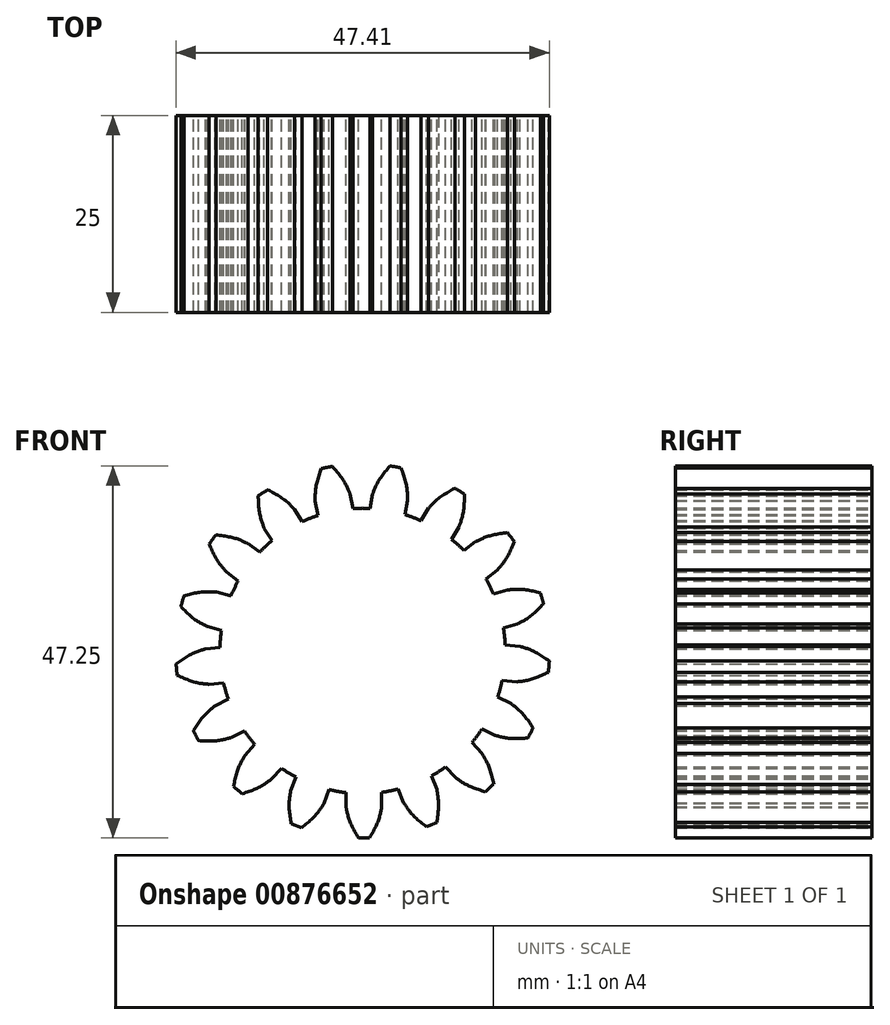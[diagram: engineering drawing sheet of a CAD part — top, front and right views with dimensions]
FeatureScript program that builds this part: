
annotation { "Feature Type Name" : "Feature", "Feature Type Description" : "" }
export const myFeature = defineFeature(function(context is Context, id is Id, definition is map)
    precondition{}
    {
        {
            var Q0;
            Q0=qCreatedBy(makeId("Front.planeOp"),FACE);
            var sketch = newSketch(context, id + "F0", { "sketchPlane" : qUnion([Q0])});
            skCircle(sketch, "E0", {"center": v(0, 0) * mm, "radius": 21.25 * mm, "construction": true});
            skCircle(sketch, "E1.0", {"center": v(0, 0) * mm, "radius": 23.75 * mm});
            skCircle(sketch, "E2.0", {"center": v(0, 0) * mm, "radius": 18.13 * mm});
            skCircle(sketch, "E3", {"center": v(0, 0) * mm, "radius": 19.97 * mm, "construction": true});
            skPoint(sketch, "E4", {"position": v(0, 21.25) * mm});
            skLineSegment(sketch, "E5", {"start": v(6.83, 18.76) * mm, "end": v(-5.25, 23.16) * mm, "construction": true});
            skLineSegment(sketch, "E6", {"start": v(-5.25, 23.16) * mm, "end": v(0, 0) * mm, "construction": true});
            skLineSegment(sketch, "E7", {"start": v(6.83, 18.76) * mm, "end": v(0, 0) * mm, "construction": true});
            skLineSegment(sketch, "E8", {"start": v(0, 0) * mm, "end": v(3.68, 19.63) * mm, "construction": true});
            skLineSegment(sketch, "E9", {"start": v(0, 0) * mm, "end": v(0.43, 19.96) * mm, "construction": true});
            skLineSegment(sketch, "E10", {"start": v(0, 0) * mm, "end": v(-2.84, 19.77) * mm, "construction": true});
            skPoint(sketch, "E11", {"position": v(-6.03, 19.04) * mm});
            skLineSegment(sketch, "E12", {"start": v(0, 0) * mm, "end": v(-6.03, 19.04) * mm, "construction": true});
            skLineSegment(sketch, "E13", {"start": v(3.68, 19.63) * mm, "end": v(-5.8, 21.4) * mm, "construction": true});
            skLineSegment(sketch, "E14", {"start": v(0.43, 19.96) * mm, "end": v(-6, 20.1) * mm, "construction": true});
            skLineSegment(sketch, "E15", {"start": v(-2.84, 19.77) * mm, "end": v(-6.02, 19.3) * mm, "construction": true});
            skFitSpline(sketch, "E16", {"points": [v(-6.03, 19.04) * mm, v(-6.02, 19.3) * mm, v(-6, 20.1) * mm, v(-5.8, 21.4) * mm, v(-5.25, 23.16) * mm], "startDerivative": vector(0.05, 1.79) * mm, "endDerivative": vector(1.8, 5.21) * mm});
            skPoint(sketch, "E17", {"position": v(-5.98, 20.4) * mm});
            skLineSegment(sketch, "E18", {"start": v(0, 0) * mm, "end": v(-5.34, 27.36) * mm, "construction": true});
            skLineSegment(sketch, "E19", {"start": v(-5.98, 20.4) * mm, "end": v(0, 0) * mm, "construction": true});
            skLineSegment(sketch, "E20", {"start": v(-6.03, 19.04) * mm, "end": v(-5.67, 17.22) * mm});
            skFitSpline(sketch, "E21.MirrorCS", {"points": [v(-1.58, 19.9) * mm, v(-1.69, 20.16) * mm, v(-2, 20.88) * mm, v(-2.68, 22.01) * mm, v(-3.85, 23.44) * mm], "startDerivative": vector(-0.72, 1.64) * mm, "endDerivative": vector(-3.62, 4.16) * mm});
            skLineSegment(sketch, "E22.MirrorCS", {"start": v(-1.58, 19.9) * mm, "end": v(-1.22, 18.08) * mm});
            skSolve(sketch);
        }
        {
            var Q0;
            {var subQ0=sQuery(id+"F0.wireOp",EDGE,"E16");Q0=makeQuery(id+"F0.imprint","IMPRINT",FACE,{"disambiguationData":[TD([[makeQuery(id+"F0.imprint","IMPRINT",EDGE,{"derivedFrom":subQ0}),-1.0]])]});}
            extrude(context, id + "F1", {"entities" : qUnion([Q0]), "depth" : 25 * mm, "offsetDistance" : 25 * mm});
        }
        {
            var Q0;
            Q0=qCreatedBy(makeId("Right.planeOp"),FACE);
            var sketch = newSketch(context, id + "F2", { "sketchPlane" : qUnion([Q0])});
            skLineSegment(sketch, "E23", {"start": v(0, 0) * mm, "end": v(-37.08, 0) * mm, "construction": true});
            skSolve(sketch);
        }
        {
            var Q0;
            Q0=makeQuery(id+"F1.opExtrude","SWEPT_BODY",BODY,{"disambiguationData":[OSD([sQuery(id+"F0.wireOp",EDGE,"E1.0"),sQuery(id+"F0.wireOp",EDGE,"E2.0"),sQuery(id+"F0.wireOp",EDGE,"E16"),sQuery(id+"F0.wireOp",EDGE,"E20"),sQuery(id+"F0.wireOp",EDGE,"E21.MirrorCS"),sQuery(id+"F0.wireOp",EDGE,"E22.MirrorCS")])]});
            var Q1;
            Q1=sQuery(id+"F2.wireOp",EDGE,"E23");
            circularPattern(context, id + "F3", {"entities" : qUnion([Q0]), "axis" : qUnion([Q1]), "angle" : 360 * degree, "instanceCount" : 17, "equalSpace" : true});
        }
        {
            var Q0;
            {var subQ0=sQuery(id+"F0.wireOp",EDGE,"E2.0");var subQ1=makeQuery(id+"F0.imprint","INTERSECT",VERTEX,{"derivedFrom":[subQ0,sQuery(id+"F0.wireOp",EDGE,"E20")]});Q0=makeQuery(id+"F0.imprint","IMPRINT",FACE,{"disambiguationData":[TD([[makeQuery(id+"F0.imprint","IMPRINT",EDGE,{"disambiguationData":[TD([[subQ1,1.0]])],"derivedFrom":subQ0}),1.0]])]});}
            extrude(context, id + "F4", {"entities" : qUnion([Q0]), "operationType" : NewBodyOperationType.ADD, "depth" : 25 * mm, "offsetDistance" : 25 * mm});
        }
    });
